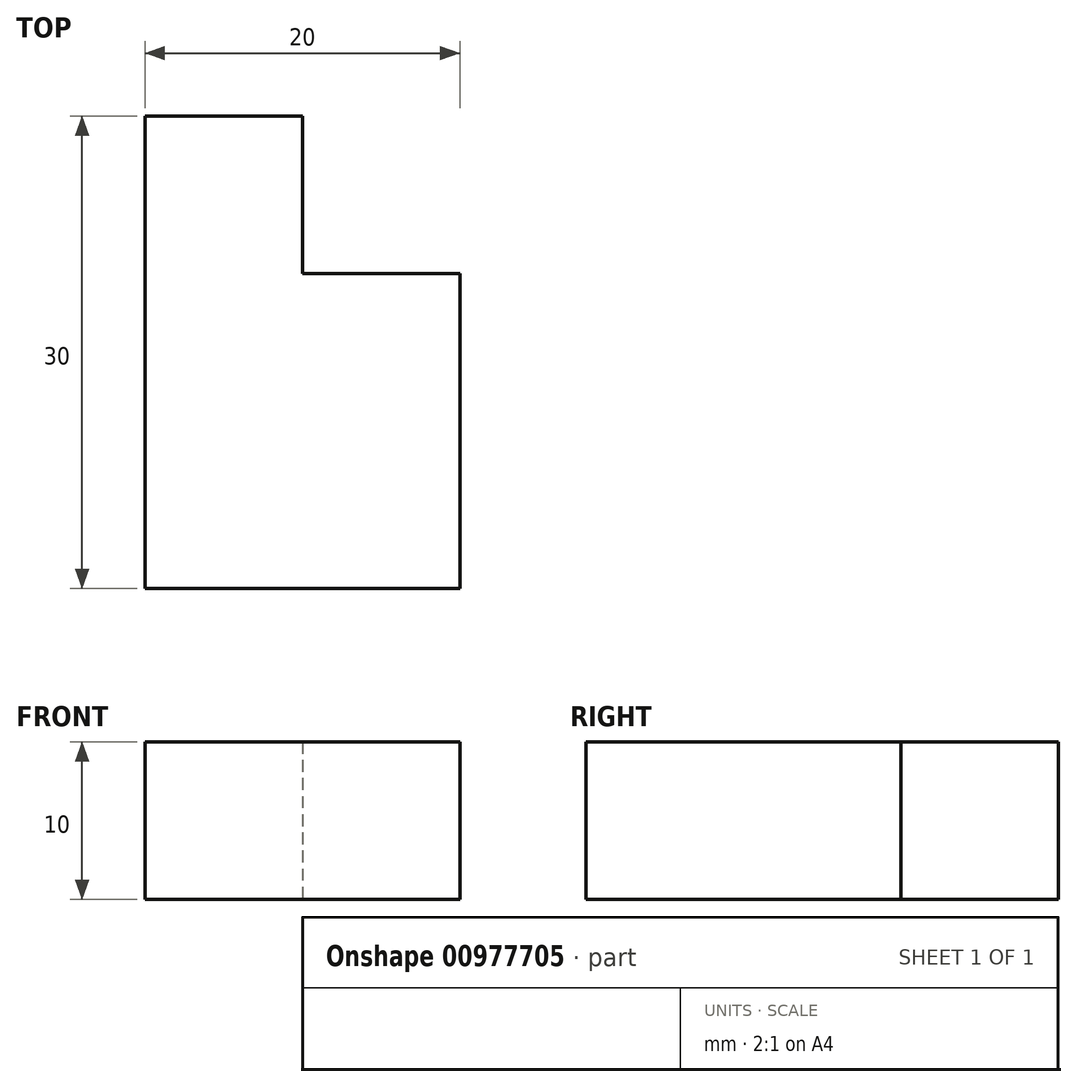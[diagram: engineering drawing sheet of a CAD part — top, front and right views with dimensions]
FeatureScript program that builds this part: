
annotation { "Feature Type Name" : "Feature", "Feature Type Description" : "" }
export const myFeature = defineFeature(function(context is Context, id is Id, definition is map)
    precondition{}
    {
        {
            var Q0;
            Q0=qCreatedBy(makeId("Top.planeOp"),FACE);
            var sketch = newSketch(context, id + "F0", { "sketchPlane" : qUnion([Q0])});
            skLineSegment(sketch, "E0.bottom", {"start": v(-10, 10) * mm, "end": v(10, 10) * mm});
            skLineSegment(sketch, "E0.top", {"start": v(-10, -10) * mm, "end": v(10, -10) * mm});
            skLineSegment(sketch, "E0.left", {"start": v(-10, 10) * mm, "end": v(-10, -10) * mm});
            skLineSegment(sketch, "E0.right", {"start": v(10, 10) * mm, "end": v(10, -10) * mm});
            skLineSegment(sketch, "E1.bottom", {"start": v(-10, 20) * mm, "end": v(0, 20) * mm});
            skLineSegment(sketch, "E1.top", {"start": v(-10, 10) * mm, "end": v(0, 10) * mm});
            skLineSegment(sketch, "E1.left", {"start": v(-10, 20) * mm, "end": v(-10, 10) * mm});
            skLineSegment(sketch, "E1.right", {"start": v(0, 20) * mm, "end": v(0, 10) * mm});
            skSolve(sketch);
        }
        {
            var Q0;
            Q0=makeQuery(id+"F0.imprint","IMPRINT",FACE,{"disambiguationData":[TD([[makeQuery(id+"F0.imprint","IMPRINT",EDGE,{"derivedFrom":sQuery(id+"F0.wireOp",EDGE,"E0.bottom")}),-1.0]])]});
            var Q1;
            Q1=makeQuery(id+"F0.imprint","IMPRINT",FACE,{"disambiguationData":[TD([[makeQuery(id+"F0.imprint","IMPRINT",EDGE,{"derivedFrom":sQuery(id+"F0.wireOp",EDGE,"E1.bottom")}),-1.0]])]});
            extrude(context, id + "F1", {"entities" : qUnion([Q0, Q1]), "depth" : 10 * mm, "offsetDistance" : 25 * mm});
        }
    });
